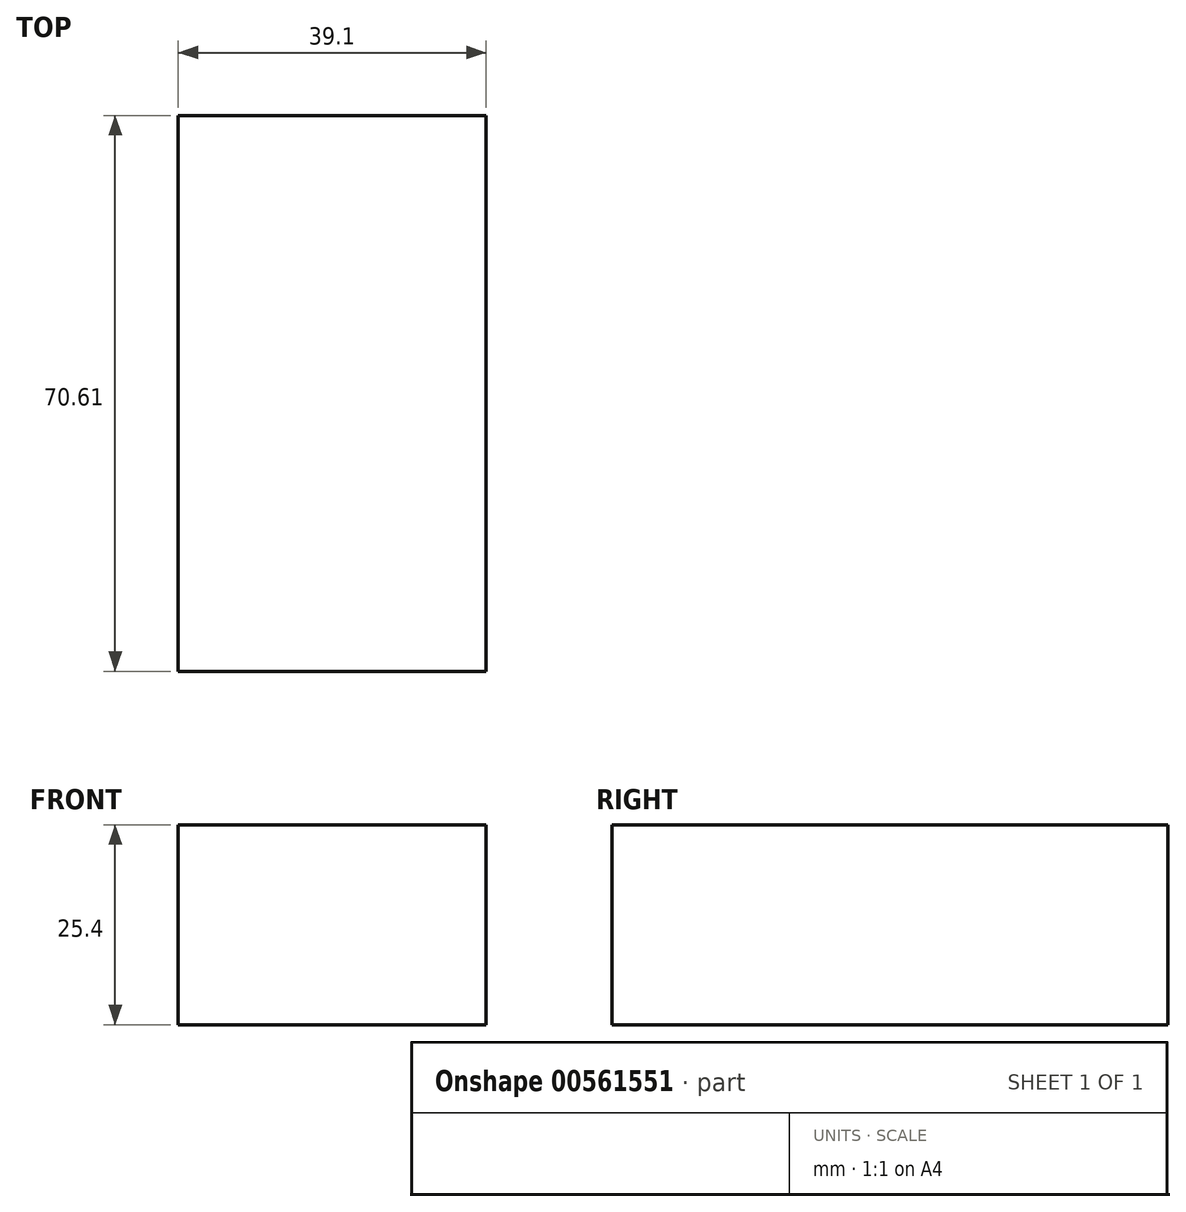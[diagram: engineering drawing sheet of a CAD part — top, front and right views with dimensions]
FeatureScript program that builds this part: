
annotation { "Feature Type Name" : "Feature", "Feature Type Description" : "" }
export const myFeature = defineFeature(function(context is Context, id is Id, definition is map)
    precondition{}
    {
        {
            var Q0;
            Q0=qCreatedBy(makeId("Front.planeOp"),FACE);
            var sketch = newSketch(context, id + "F0", { "sketchPlane" : qUnion([Q0])});
            skCircle(sketch, "E0", {"center": v(-56.37, 0) * mm, "radius": 23.6 * mm});
            skSolve(sketch);
        }
        {
            var Q0;
            Q0=sQuery(id+"F0.wireOp",EDGE,"E0");
            extrude(context, id + "F1", {"bodyType" : ToolBodyType.SURFACE, "surfaceEntities" : qUnion([Q0]), "depth" : 25.4 * mm, "offsetDistance" : 25.4 * mm});
        }
        {
            var Q0;
            Q0=qCreatedBy(makeId("Top.planeOp"),FACE);
            var sketch = newSketch(context, id + "F2", { "sketchPlane" : qUnion([Q0])});
            skLineSegment(sketch, "E1.bottom", {"start": v(94.03, 44.3) * mm, "end": v(133.13, 44.3) * mm});
            skLineSegment(sketch, "E1.top", {"start": v(94.03, -26.3) * mm, "end": v(133.13, -26.3) * mm});
            skLineSegment(sketch, "E1.left", {"start": v(94.03, 44.3) * mm, "end": v(94.03, -26.3) * mm});
            skLineSegment(sketch, "E1.right", {"start": v(133.13, 44.3) * mm, "end": v(133.13, -26.3) * mm});
            skSolve(sketch);
        }
        {
            var Q0;
            Q0 = qSketchRegion(id + "F2", true);
            extrude(context, id + "F3", {"entities" : qUnion([Q0]), "depth" : 25.4 * mm, "offsetDistance" : 25.4 * mm});
        }
    });
